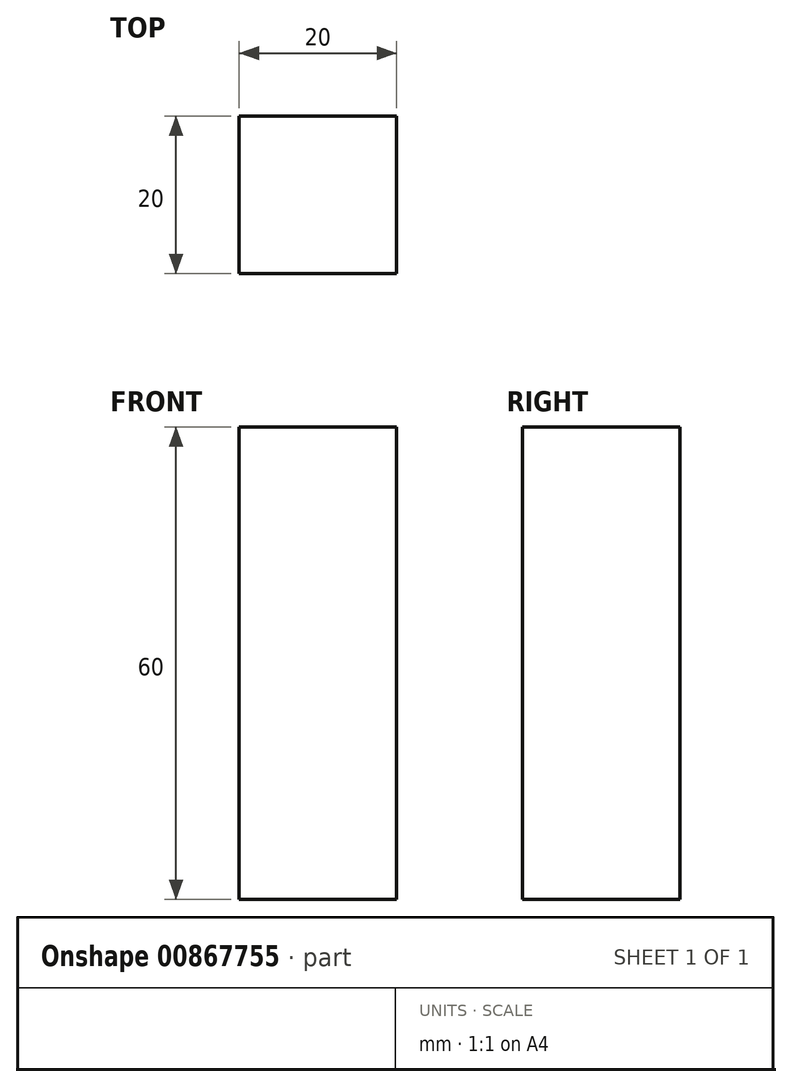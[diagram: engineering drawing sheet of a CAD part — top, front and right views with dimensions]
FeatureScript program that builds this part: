
annotation { "Feature Type Name" : "Feature", "Feature Type Description" : "" }
export const myFeature = defineFeature(function(context is Context, id is Id, definition is map)
    precondition{}
    {
        {
            var Q0;
            Q0=qCreatedBy(makeId("Top.planeOp"),FACE);
            var sketch = newSketch(context, id + "F0", { "sketchPlane" : qUnion([Q0])});
            skLineSegment(sketch, "E0.bottom", {"start": v(10, -10) * mm, "end": v(-10, -10) * mm});
            skLineSegment(sketch, "E0.top", {"start": v(10, 10) * mm, "end": v(-10, 10) * mm});
            skLineSegment(sketch, "E0.left", {"start": v(10, -10) * mm, "end": v(10, 10) * mm});
            skLineSegment(sketch, "E0.right", {"start": v(-10, -10) * mm, "end": v(-10, 10) * mm});
            skPoint(sketch, "E0.middle", {"position": v(0, 0) * mm});
            skLineSegment(sketch, "E1.0", {"start": v(9.6, 9.6) * mm, "end": v(-9.6, 9.6) * mm});
            skLineSegment(sketch, "E1.1", {"start": v(9.6, -9.6) * mm, "end": v(9.6, 9.6) * mm});
            skLineSegment(sketch, "E1.2", {"start": v(9.6, -9.6) * mm, "end": v(-9.6, -9.6) * mm});
            skLineSegment(sketch, "E1.3", {"start": v(-9.6, -9.6) * mm, "end": v(-9.6, 9.6) * mm});
            skSolve(sketch);
        }
        {
            var Q0;
            Q0=makeQuery(id+"F0.imprint","IMPRINT",FACE,{"disambiguationData":[TD([[makeQuery(id+"F0.imprint","IMPRINT",EDGE,{"derivedFrom":sQuery(id+"F0.wireOp",EDGE,"E1.0")}),1.0]])]});
            var Q1;
            Q1=makeQuery(id+"F0.imprint","IMPRINT",FACE,{"disambiguationData":[TD([[makeQuery(id+"F0.imprint","IMPRINT",EDGE,{"derivedFrom":sQuery(id+"F0.wireOp",EDGE,"E0.bottom")}),-1.0]])]});
            extrude(context, id + "F1", {"entities" : qUnion([Q0, Q1]), "depth" : 60 * mm, "offsetDistance" : 25 * mm});
        }
    });
